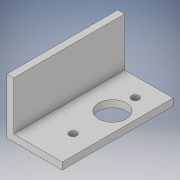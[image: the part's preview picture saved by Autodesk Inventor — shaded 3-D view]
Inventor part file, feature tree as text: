
AUTODESK INVENTOR PART (.ipt)
format: ipt  version: 2018 (Build 220112000, 112)  size: 119,808 bytes
history: native  units: in
note: dims shown in document units (in); Inventor stores cm internally (conversion verified against a paired STEP export)
features: extrude x3, sketch x2
ambient origin geometry x8: Origin, YZ Plane, XZ Plane, XY Plane, X Axis, Y Axis, Z Axis, Center Point
bodies: Solid1 (feature_tree)
feature tree (5):
  extrude  "Extrusion1"  Depth=1.0in
  extrude  "Extrusion2"  Depth=0.125in
  extrude  "Extrusion3"  Depth=2.0in TaperAngle=0.0deg
  sketch  "Sketch1"  dims[d0=0.125in d1=1.0in]
  sketch  "Sketch3"  dims[d2=1.0in d3=0.125in d4=2.0in d5=0.0in d6=0.655in d9=0.5in d10=2.0in d11=0.0in d12=0.75in d13=0.413in d14=1.122in d15=0.134in d16=1.0in d17=0.0in]
